# Revit family: EKF_EE_КомплектРеекДляМонтажнойРамыДвери(4шт)Trivia_AVERES
name_source: partatom
category: Электрооборудование
units: mm (PartAtom-declared; Revit-internal decimal feet)

## family parameters
Всегда вертикально = Нет
На основе рабочей плоскости = Да
Общий = Да
При загрузке вырезать с полостями = Нет
Размер круглого соединителя = Использовать диаметр
Тип детали = Силовой щит
Точка расчета площади = Нет

## types (3) — shared parameters
ADSK_Единица измерения = шт.
ADSK_Завод-изготовитель = EKF
ADSK_Количество = 1
ADSK_Материал = RAL 7035_Сталь
ADSK_Размер_Высота = 20 мм
ADSK_Размер_Глубина = 12 мм
Изготовитель = EKF
Серия номенклатуры = Averes
Степень защиты IP = -
ТВ = EKF_2_TRIVIA_AVERES
Тип установки = -
zero-valued in all types: ADSK_Масса, Отметка по умолчанию

## per-type parameters (varying)
| type | ADSK_Код изделия | ADSK_Марка | ADSK_Наименование | ADSK_Обозначение | ADSK_Размер_Ширина | Тип |
| Комплект реек для монтажной рамы двери Ш800 мм (4шт) EKF AVERES | AFR800 | Комплект реек для монтажной рамы двери Ш800 мм (4 шт) EKF AVERES | Комплект реек для монтажной рамы двери Ш800 мм (4 шт) EKF AVERES | Комплект реек для монтажной рамы двери Ш800 мм (4 шт) EKF AVERES | 600 мм | 658 мм |
| Комплект реек для монтажной рамы двери Ш600 мм (4шт) EKF AVERES | AFR600 | Комплект реек для монтажной рамы двери Ш600 мм (4 шт) EKF AVERES | Комплект реек для монтажной рамы двери Ш600 мм (4 шт) EKF AVERES | Комплект реек для монтажной рамы двери Ш600 мм (4 шт) EKF AVERES | 400 мм | 657 мм |
| Комплект реек для монтажной рамы двери Ш400 мм (4шт) EKF AVERES | AFR400 | Комплект реек для монтажной рамы двери Ш400 мм (4 шт) EKF AVERES | Комплект реек для монтажной рамы двери Ш400 мм (4 шт) EKF AVERES | Комплект реек для монтажной рамы двери Ш400 мм (4 шт) EKF AVERES | 200 мм | 656 мм |
